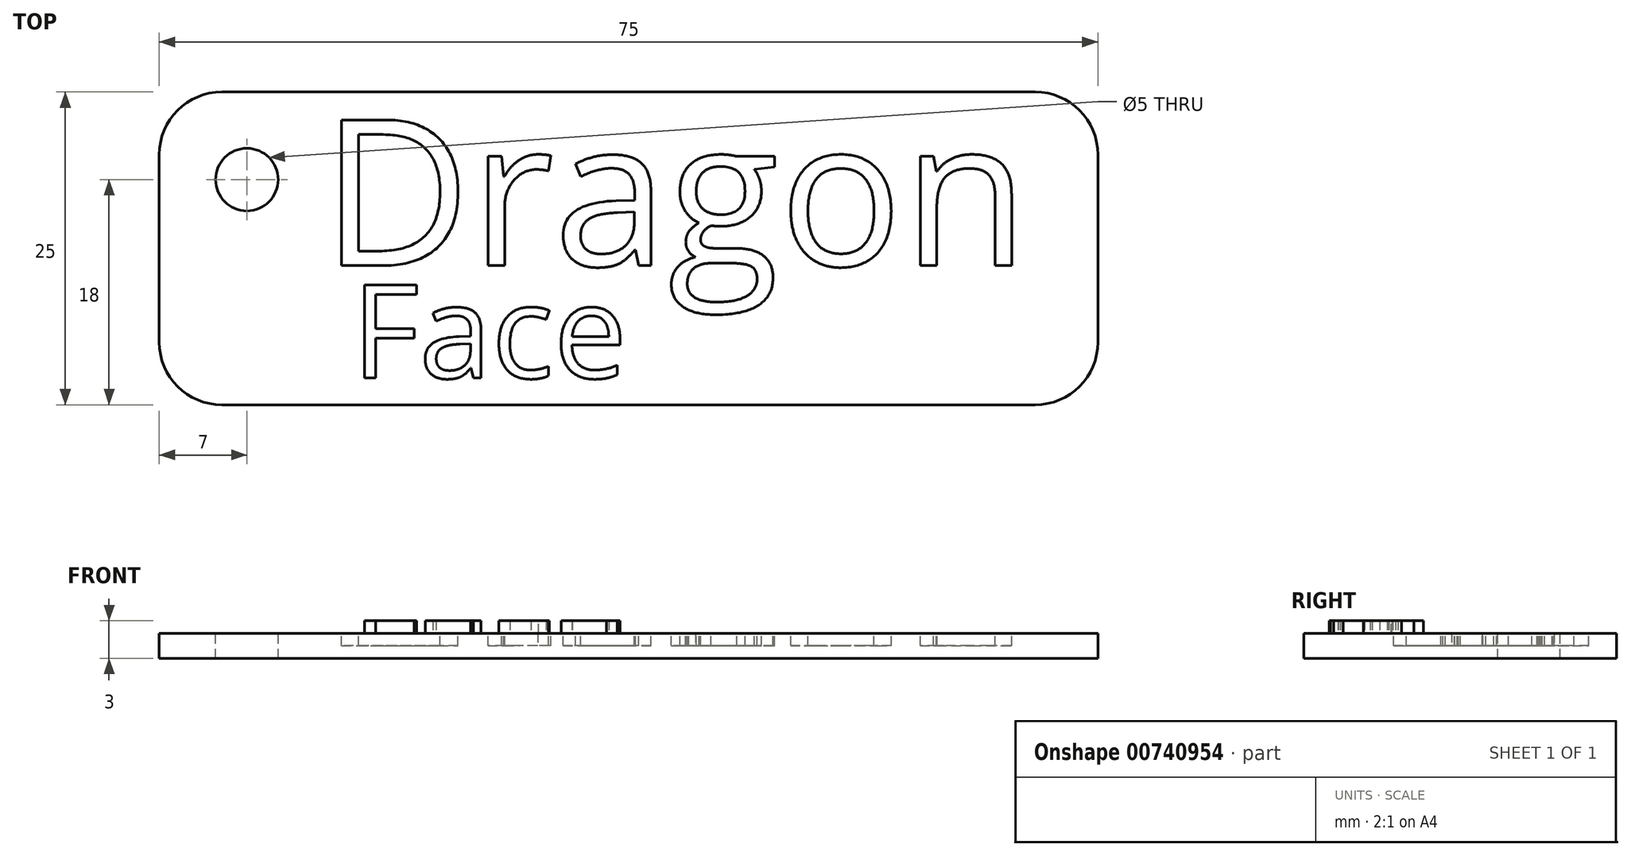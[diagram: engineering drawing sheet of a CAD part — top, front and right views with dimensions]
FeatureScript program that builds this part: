
annotation { "Feature Type Name" : "Feature", "Feature Type Description" : "" }
export const myFeature = defineFeature(function(context is Context, id is Id, definition is map)
    precondition{}
    {
        {
            var Q0;
            Q0=qCreatedBy(makeId("Top.planeOp"),FACE);
            var sketch = newSketch(context, id + "F0", { "sketchPlane" : qUnion([Q0])});
            skLineSegment(sketch, "E0.bottom", {"start": v(-32.5, 12.5) * mm, "end": v(32.5, 12.5) * mm});
            skLineSegment(sketch, "E0.top", {"start": v(-32.5, -12.5) * mm, "end": v(32.5, -12.5) * mm});
            skLineSegment(sketch, "E0.left", {"start": v(-37.5, 7.5) * mm, "end": v(-37.5, -7.5) * mm});
            skLineSegment(sketch, "E0.right", {"start": v(37.5, 7.5) * mm, "end": v(37.5, -7.5) * mm});
            skPoint(sketch, "E0.middle", {"position": v(0, 0) * mm});
            skPoint(sketch, "E1.visualSharp", {"position": v(-37.5, 12.5) * mm});
            skArc(sketch, "E1.filletArc", {"start": v(-32.5, 12.5) * mm, "mid": v(-36.04, 11.04) * mm, "end": v(-37.5, 7.5) * mm});
            skPoint(sketch, "E2.visualSharp", {"position": v(37.5, 12.5) * mm});
            skArc(sketch, "E2.filletArc", {"start": v(37.5, 7.5) * mm, "mid": v(36.04, 11.04) * mm, "end": v(32.5, 12.5) * mm});
            skPoint(sketch, "E3.visualSharp", {"position": v(37.5, -12.5) * mm});
            skArc(sketch, "E3.filletArc", {"start": v(32.5, -12.5) * mm, "mid": v(36.04, -11.04) * mm, "end": v(37.5, -7.5) * mm});
            skPoint(sketch, "E4.visualSharp", {"position": v(-37.5, -12.5) * mm});
            skArc(sketch, "E4.filletArc", {"start": v(-37.5, -7.5) * mm, "mid": v(-36.04, -11.04) * mm, "end": v(-32.5, -12.5) * mm});
            skSolve(sketch);
        }
        {
            var Q0;
            Q0=makeQuery(id+"F0.imprint","IMPRINT",FACE,{"disambiguationData":[TD([[makeQuery(id+"F0.imprint","IMPRINT",EDGE,{"derivedFrom":sQuery(id+"F0.wireOp",EDGE,"E0.bottom")}),-1.0]])]});
            extrude(context, id + "F1", {"entities" : qUnion([Q0]), "depth" : 2 * mm, "offsetDistance" : 25 * mm});
        }
        {
            var Q0;
            Q0=makeQuery(id+"F1.opExtrude","CAP_FACE",FACE,{"disambiguationData":[OSD([sQuery(id+"F0.wireOp",EDGE,"E0.bottom"),sQuery(id+"F0.wireOp",EDGE,"E0.top"),sQuery(id+"F0.wireOp",EDGE,"E0.left"),sQuery(id+"F0.wireOp",EDGE,"E0.right"),sQuery(id+"F0.wireOp",EDGE,"E1.filletArc"),sQuery(id+"F0.wireOp",EDGE,"E2.filletArc"),sQuery(id+"F0.wireOp",EDGE,"E3.filletArc"),sQuery(id+"F0.wireOp",EDGE,"E4.filletArc")])],"isStart":false});
            var sketch = newSketch(context, id + "F2", { "sketchPlane" : qUnion([Q0])});
            skPoint(sketch, "E5", {"position": v(-30.5, 5.5) * mm});
            skSolve(sketch);
        }
        {
            var Q0;
            Q0=sQuery(id+"F2.wireOp",VERTEX,"E5");
            var Q1;
            Q1=makeQuery(id+"F1.opExtrude","SWEPT_BODY",BODY,{"disambiguationData":[OSD([sQuery(id+"F0.wireOp",EDGE,"E0.bottom"),sQuery(id+"F0.wireOp",EDGE,"E0.top"),sQuery(id+"F0.wireOp",EDGE,"E0.left"),sQuery(id+"F0.wireOp",EDGE,"E0.right"),sQuery(id+"F0.wireOp",EDGE,"E1.filletArc"),sQuery(id+"F0.wireOp",EDGE,"E2.filletArc"),sQuery(id+"F0.wireOp",EDGE,"E3.filletArc"),sQuery(id+"F0.wireOp",EDGE,"E4.filletArc")])]});
            hole(context, id + "F3", {"style" : HoleStyle.SIMPLE, "endStyle" : HoleEndStyle.THROUGH, "holeDiameter" : 5 * mm, "majorDiameter" : 5 * mm, "isTappedThrough" : true, "tappedDepth" : 12 * mm, "tapClearance" : 3, "locations" : qUnion([Q0]), "scope" : qUnion([Q1])});
        }
        {
            var Q0;
            Q0=makeQuery(id+"F1.opExtrude","CAP_FACE",FACE,{"disambiguationData":[OSD([sQuery(id+"F0.wireOp",EDGE,"E0.bottom"),sQuery(id+"F0.wireOp",EDGE,"E0.top"),sQuery(id+"F0.wireOp",EDGE,"E0.left"),sQuery(id+"F0.wireOp",EDGE,"E0.right"),sQuery(id+"F0.wireOp",EDGE,"E1.filletArc"),sQuery(id+"F0.wireOp",EDGE,"E2.filletArc"),sQuery(id+"F0.wireOp",EDGE,"E3.filletArc"),sQuery(id+"F0.wireOp",EDGE,"E4.filletArc")])],"isStart":false});
            var sketch = newSketch(context, id + "F4", { "sketchPlane" : qUnion([Q0])});
            skText(sketch, "E6", { "text": "Dragon", "fontName": "OpenSans-Regular.ttf"});
            const initialGuessF4  = {"E6": [-0.02453, -0.00138, 1, 0, 0.01175]};
            skSetInitialGuess(sketch, initialGuessF4);
            skSolve(sketch);
        }
        {
            var Q0;
            Q0 = qSketchRegion(id + "F4", true);
            extrude(context, id + "F5", {"entities" : qUnion([Q0]), "operationType" : NewBodyOperationType.REMOVE, "oppositeDirection" : true, "depth" : 1 * mm, "offsetDistance" : 25 * mm});
        }
        {
            var Q0;
            {var subQ0=sQuery(id+"F0.wireOp",EDGE,"E1.filletArc");var subQ1=sQuery(id+"F0.wireOp",EDGE,"E0.right");var subQ2=sQuery(id+"F0.wireOp",EDGE,"E0.top");var subQ3=sQuery(id+"F0.wireOp",EDGE,"E0.bottom");var subQ4=sQuery(id+"F0.wireOp",EDGE,"E2.filletArc");var subQ5=sQuery(id+"F0.wireOp",EDGE,"E0.left");var subQ6=sQuery(id+"F0.wireOp",EDGE,"E3.filletArc");var subQ7=sQuery(id+"F0.wireOp",EDGE,"E4.filletArc");Q0=makeQuery(id+"F5.boolean.opBoolean","SPLIT",FACE,{"disambiguationData":[TD([makeQuery(id+"F1.opExtrude","SWEPT_FACE",FACE,{"disambiguationData":[OSD([subQ3])]})])],"derivedFrom":makeQuery(id+"F1.opExtrude","CAP_FACE",FACE,{"disambiguationData":[OSD([subQ3,subQ2,subQ5,subQ1,subQ0,subQ4,subQ6,subQ7])],"isStart":false})});}
            var sketch = newSketch(context, id + "F6", { "sketchPlane" : qUnion([Q0])});
            skText(sketch, "E7", { "text": "Face", "fontName": "OpenSans-Regular.ttf"});
            const initialGuessF6  = {"E7": [-0.02211, -0.01036, 1, 0, 0.0075]};
            skSetInitialGuess(sketch, initialGuessF6);
            skSolve(sketch);
        }
        {
            var Q0;
            Q0 = qSketchRegion(id + "F6", true);
            extrude(context, id + "F7", {"entities" : qUnion([Q0]), "operationType" : NewBodyOperationType.ADD, "depth" : 1 * mm, "offsetDistance" : 25 * mm});
        }
    });
